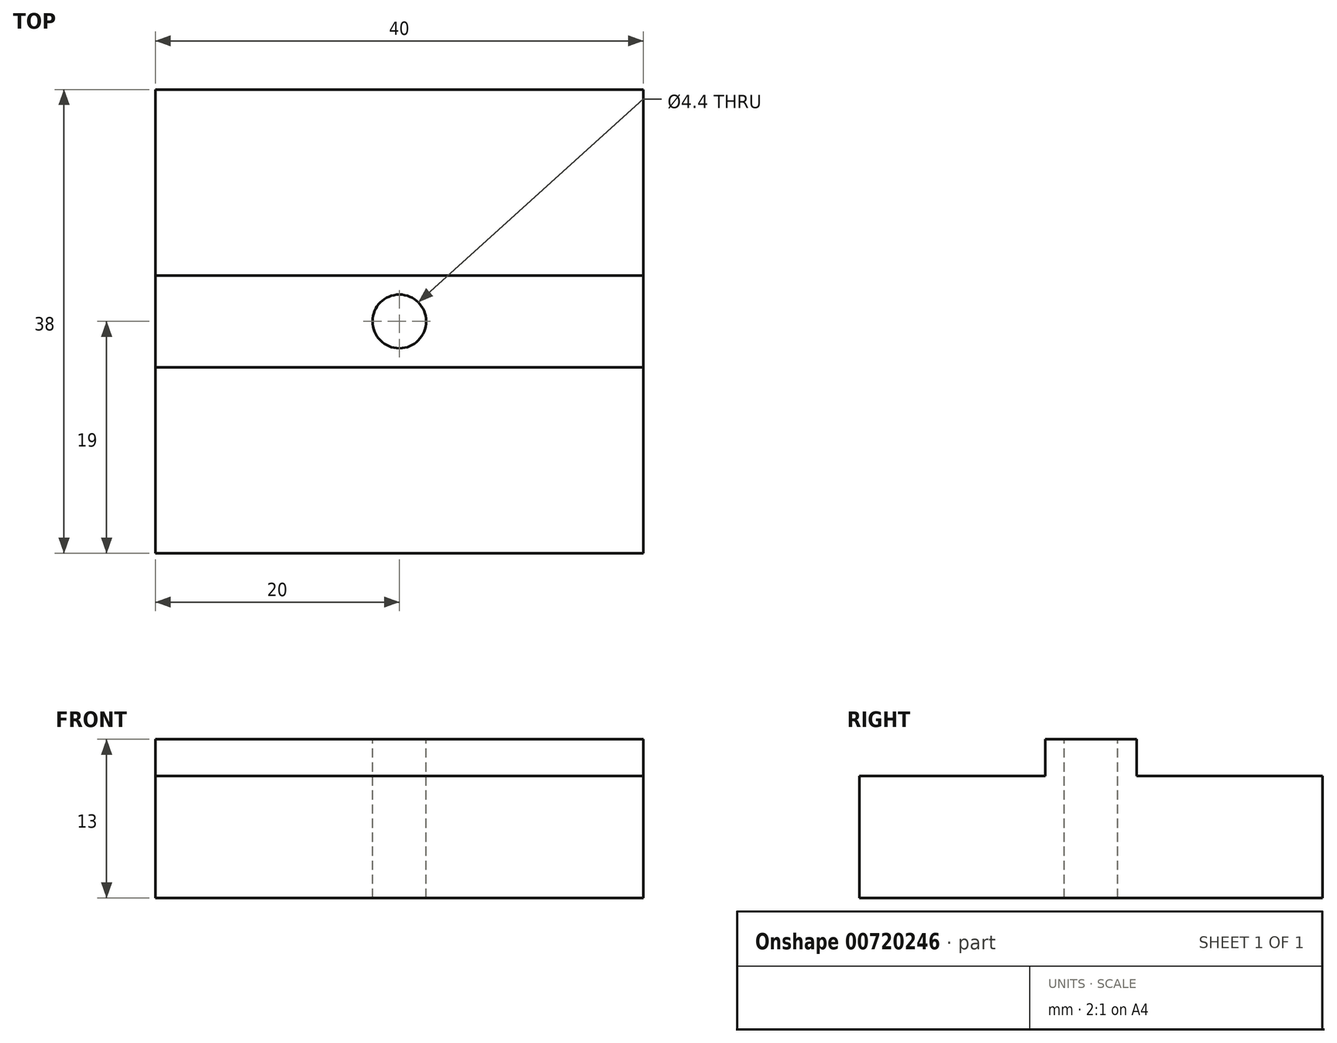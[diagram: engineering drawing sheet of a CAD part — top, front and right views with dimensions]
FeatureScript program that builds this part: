
annotation { "Feature Type Name" : "Feature", "Feature Type Description" : "" }
export const myFeature = defineFeature(function(context is Context, id is Id, definition is map)
    precondition{}
    {
        {
            var Q0;
            Q0=qCreatedBy(makeId("Top.planeOp"),FACE);
            var sketch = newSketch(context, id + "F0", { "sketchPlane" : qUnion([Q0])});
            skLineSegment(sketch, "E0.bottom", {"start": v(20, 19) * mm, "end": v(-20, 19) * mm});
            skLineSegment(sketch, "E0.top", {"start": v(20, -19) * mm, "end": v(-20, -19) * mm});
            skLineSegment(sketch, "E0.left", {"start": v(20, 19) * mm, "end": v(20, -19) * mm});
            skLineSegment(sketch, "E0.right", {"start": v(-20, 19) * mm, "end": v(-20, -19) * mm});
            skPoint(sketch, "E0.middle", {"position": v(0, 0) * mm});
            skLineSegment(sketch, "E1.bottom", {"start": v(20, 3.75) * mm, "end": v(-20, 3.75) * mm});
            skLineSegment(sketch, "E1.top", {"start": v(20, -3.75) * mm, "end": v(-20, -3.75) * mm});
            skLineSegment(sketch, "E1.left", {"start": v(20, 3.75) * mm, "end": v(20, -3.75) * mm});
            skLineSegment(sketch, "E1.right", {"start": v(-20, 3.75) * mm, "end": v(-20, -3.75) * mm});
            skLineSegment(sketch, "E2", {"start": v(0, -19) * mm, "end": v(0, 19) * mm});
            skSolve(sketch);
        }
        {
            var Q0;
            {var subQ0=sQuery(id+"F0.wireOp",EDGE,"E0.bottom");Q0=makeQuery(id+"F0.imprint","IMPRINT",FACE,{"disambiguationData":[TD([[makeQuery(id+"F0.imprint","IMPRINT",EDGE,{"derivedFrom":subQ0}),1.0]])]});}
            var Q1;
            {var subQ0=sQuery(id+"F0.wireOp",EDGE,"E0.top");Q1=makeQuery(id+"F0.imprint","IMPRINT",FACE,{"disambiguationData":[TD([[makeQuery(id+"F0.imprint","IMPRINT",EDGE,{"derivedFrom":subQ0}),-1.0]])]});}
            var Q2;
            Q2=makeQuery(id+"F0.imprint","IMPRINT",FACE,{"disambiguationData":[TD([[makeQuery(id+"F0.imprint","IMPRINT",EDGE,{"derivedFrom":sQuery(id+"F0.wireOp",EDGE,"E1.bottom")}),1.0]])]});
            extrude(context, id + "F1", {"entities" : qUnion([Q0, Q1, Q2]), "oppositeDirection" : true, "depth" : 10 * mm, "offsetDistance" : 25 * mm});
        }
        {
            var Q0;
            Q0=makeQuery(id+"F0.imprint","IMPRINT",FACE,{"disambiguationData":[TD([[makeQuery(id+"F0.imprint","IMPRINT",EDGE,{"derivedFrom":sQuery(id+"F0.wireOp",EDGE,"E1.bottom")}),1.0]])]});
            extrude(context, id + "F2", {"entities" : qUnion([Q0]), "operationType" : NewBodyOperationType.ADD, "depth" : 3 * mm, "offsetDistance" : 25 * mm});
        }
        {
            var Q0;
            Q0=makeQuery(id+"F1.opExtrude","CAP_FACE",FACE,{"disambiguationData":[OSD([sQuery(id+"F0.wireOp",EDGE,"E0.bottom"),sQuery(id+"F0.wireOp",EDGE,"E0.top"),sQuery(id+"F0.wireOp",EDGE,"E0.left"),sQuery(id+"F0.wireOp",EDGE,"E0.right"),sQuery(id+"F0.wireOp",EDGE,"E1.left"),sQuery(id+"F0.wireOp",EDGE,"E1.right")])],"isStart":false});
            var sketch = newSketch(context, id + "F3", { "sketchPlane" : qUnion([Q0])});
            skPoint(sketch, "E3", {"position": v(0, 0) * mm});
            skSolve(sketch);
        }
        {
            var Q0;
            Q0=sQuery(id+"F3.wireOp",VERTEX,"E3");
            var Q1;
            Q1=makeQuery(id+"F1.opExtrude","SWEPT_BODY",BODY,{"disambiguationData":[OSD([sQuery(id+"F0.wireOp",EDGE,"E0.bottom"),sQuery(id+"F0.wireOp",EDGE,"E0.top"),sQuery(id+"F0.wireOp",EDGE,"E0.left"),sQuery(id+"F0.wireOp",EDGE,"E0.right"),sQuery(id+"F0.wireOp",EDGE,"E1.left"),sQuery(id+"F0.wireOp",EDGE,"E1.right")])]});
            hole(context, id + "F4", {"style" : HoleStyle.SIMPLE, "endStyle" : HoleEndStyle.BLIND, "holeDiameter" : 4.4 * mm, "majorDiameter" : 5 * mm, "holeDepth" : 20 * mm, "tappedDepth" : 12 * mm, "tapClearance" : 3, "locations" : qUnion([Q0]), "scope" : qUnion([Q1])});
        }
    });
